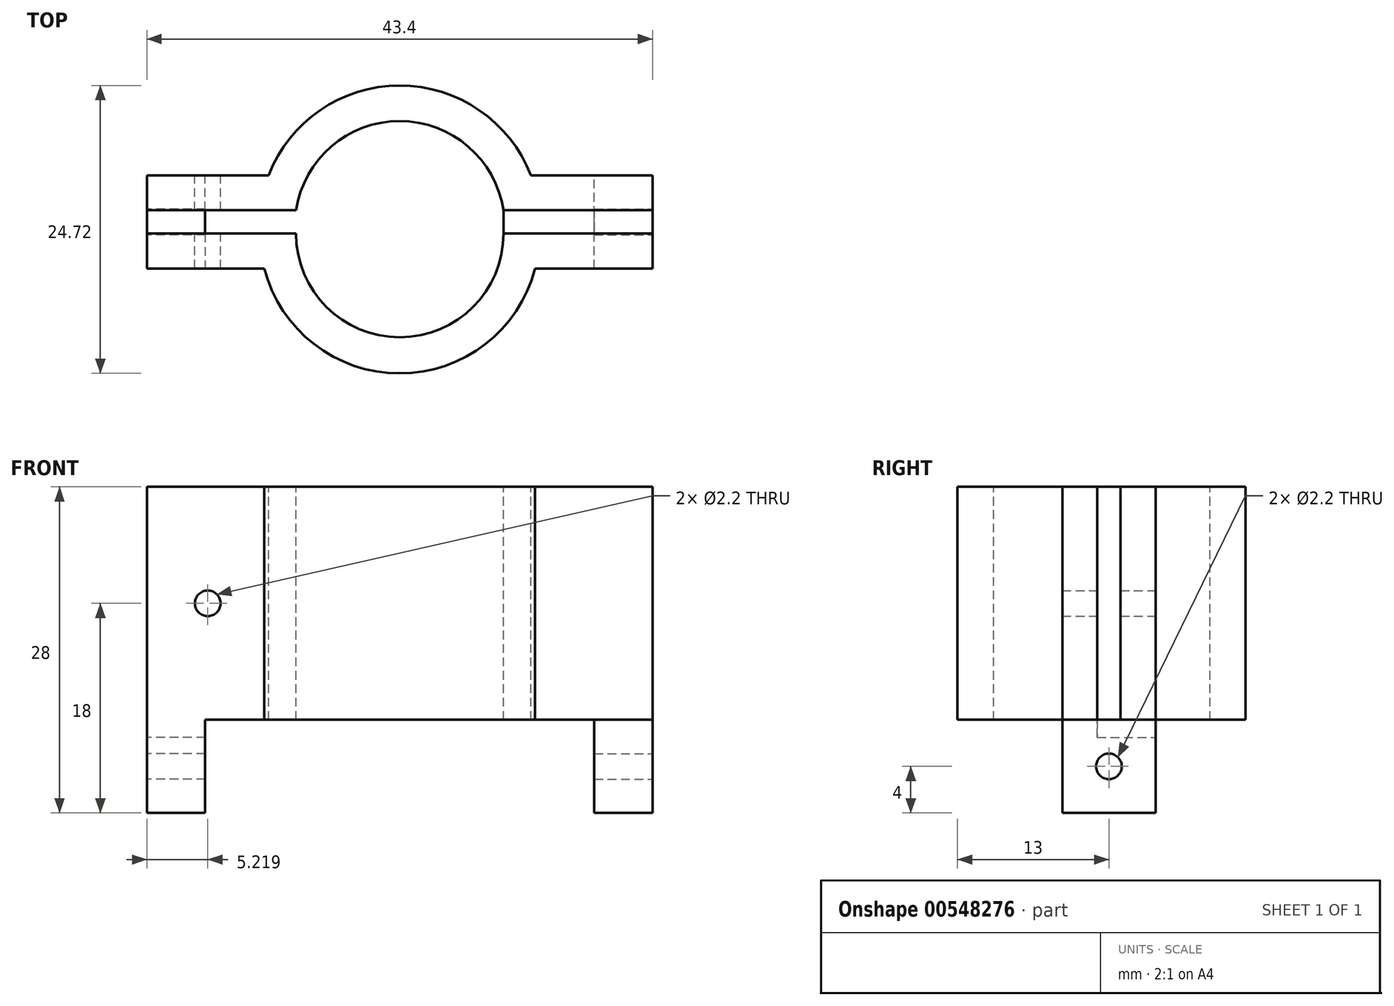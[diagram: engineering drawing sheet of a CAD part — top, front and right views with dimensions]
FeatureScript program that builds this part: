
annotation { "Feature Type Name" : "Feature", "Feature Type Description" : "" }
export const myFeature = defineFeature(function(context is Context, id is Id, definition is map)
    precondition{}
    {
        {
            var Q0;
            Q0=qCreatedBy(makeId("Top.planeOp"),FACE);
            var sketch = newSketch(context, id + "F0", { "sketchPlane" : qUnion([Q0])});
            skArc(sketch, "E0", {"start": v(-8.9, 0) * mm, "mid": v(0, -8.9) * mm, "end": v(8.9, 0) * mm});
            skArc(sketch, "E1", {"start": v(-12, 0) * mm, "mid": v(0, -12) * mm, "end": v(12, 0) * mm});
            skLineSegment(sketch, "E2.bottom", {"start": v(-8.9, 0) * mm, "end": v(-21.7, 0) * mm});
            skLineSegment(sketch, "E2.top", {"start": v(-8.9, -3) * mm, "end": v(-21.7, -3) * mm});
            skLineSegment(sketch, "E2.left", {"start": v(-8.9, 0) * mm, "end": v(-8.9, -3) * mm});
            skLineSegment(sketch, "E2.right", {"start": v(-21.7, 0) * mm, "end": v(-21.7, -3) * mm});
            skLineSegment(sketch, "E3.bottom", {"start": v(8.9, 0) * mm, "end": v(21.7, 0) * mm});
            skLineSegment(sketch, "E3.top", {"start": v(8.9, -3) * mm, "end": v(21.7, -3) * mm});
            skLineSegment(sketch, "E3.left", {"start": v(8.9, 0) * mm, "end": v(8.9, -3) * mm});
            skLineSegment(sketch, "E3.right", {"start": v(21.7, 0) * mm, "end": v(21.7, -3) * mm});
            skSolve(sketch);
        }
        {
            var Q0;
            Q0=qSketchRegion(id+"F0",true);
            extrude(context, id + "F1", {"entities" : qUnion([Q0]), "oppositeDirection" : true, "depth" : 20 * mm, "offsetDistance" : 25 * mm});
        }
        {
            var Q0;
            Q0=makeQuery(id+"F1.opExtrude","SWEPT_FACE",FACE,{"disambiguationData":[OSD([sQuery(id+"F0.wireOp",EDGE,"E3.right")])]});
            var sketch = newSketch(context, id + "F2", { "sketchPlane" : qUnion([Q0])});
            skPoint(sketch, "E4.oppositeSnap0", {"position": v(-1.5, 0) * mm});
            skLineSegment(sketch, "E4.bottom", {"start": v(0, -20) * mm, "end": v(2, -20) * mm});
            skLineSegment(sketch, "E4.top", {"start": v(0, 0) * mm, "end": v(2, 0) * mm});
            skLineSegment(sketch, "E4.left", {"start": v(0, -20) * mm, "end": v(0, 0) * mm});
            skLineSegment(sketch, "E4.right", {"start": v(2, -20) * mm, "end": v(2, 0) * mm});
            skLineSegment(sketch, "E5.bottom", {"start": v(-3, -20) * mm, "end": v(5, -20) * mm});
            skLineSegment(sketch, "E5.top", {"start": v(-3, -28) * mm, "end": v(5, -28) * mm});
            skLineSegment(sketch, "E5.left", {"start": v(-3, -20) * mm, "end": v(-3, -28) * mm});
            skLineSegment(sketch, "E5.right", {"start": v(5, -20) * mm, "end": v(5, -28) * mm});
            skCircle(sketch, "E6", {"center": v(1, -24) * mm, "radius": 1.1 * mm});
            skSolve(sketch);
        }
        {
            var Q0;
            Q0=qCreatedBy(makeId("Top.planeOp"),FACE);
            var sketch = newSketch(context, id + "F3", { "sketchPlane" : qUnion([Q0])});
            skArc(sketch, "E7", {"start": v(8.9, 2) * mm, "mid": v(0, 9.66) * mm, "end": v(-8.9, 2) * mm});
            skLineSegment(sketch, "E8.bottom", {"start": v(-8.9, 2) * mm, "end": v(-21.7, 2) * mm});
            skLineSegment(sketch, "E8.top", {"start": v(-8.9, 5) * mm, "end": v(-21.7, 5) * mm});
            skLineSegment(sketch, "E8.left", {"start": v(-8.9, 2) * mm, "end": v(-8.9, 5) * mm});
            skLineSegment(sketch, "E8.right", {"start": v(-21.7, 2) * mm, "end": v(-21.7, 5) * mm});
            skLineSegment(sketch, "E9.bottom", {"start": v(8.9, 2) * mm, "end": v(21.7, 2) * mm});
            skLineSegment(sketch, "E9.top", {"start": v(8.9, 5) * mm, "end": v(21.7, 5) * mm});
            skLineSegment(sketch, "E9.left", {"start": v(8.9, 2) * mm, "end": v(8.9, 5) * mm});
            skLineSegment(sketch, "E9.right", {"start": v(21.7, 2) * mm, "end": v(21.7, 5) * mm});
            skArc(sketch, "E10", {"start": v(12, 2) * mm, "mid": v(0, 12.72) * mm, "end": v(-12, 2) * mm});
            skSolve(sketch);
        }
        {
            var Q0;
            {var subQ0=sQuery(id+"F3.wireOp",EDGE,"E8.right");Q0=makeQuery(id+"F3.imprint","IMPRINT",FACE,{"disambiguationData":[TD([[makeQuery(id+"F3.imprint","IMPRINT",EDGE,{"derivedFrom":subQ0}),-1.0]])]});}
            var Q1;
            {var subQ0=sQuery(id+"F3.wireOp",EDGE,"E8.left");Q1=makeQuery(id+"F3.imprint","IMPRINT",FACE,{"disambiguationData":[TD([[makeQuery(id+"F3.imprint","IMPRINT",EDGE,{"derivedFrom":subQ0}),1.0]])]});}
            var Q2;
            Q2=makeQuery(id+"F3.imprint","IMPRINT",FACE,{"disambiguationData":[TD([[makeQuery(id+"F3.imprint","IMPRINT",EDGE,{"derivedFrom":sQuery(id+"F3.wireOp",EDGE,"E7")}),-1.0]])]});
            var Q3;
            {var subQ0=sQuery(id+"F3.wireOp",EDGE,"E9.right");Q3=makeQuery(id+"F3.imprint","IMPRINT",FACE,{"disambiguationData":[TD([[makeQuery(id+"F3.imprint","IMPRINT",EDGE,{"derivedFrom":subQ0}),1.0]])]});}
            var Q4;
            {var subQ0=sQuery(id+"F3.wireOp",EDGE,"E9.left");Q4=makeQuery(id+"F3.imprint","IMPRINT",FACE,{"disambiguationData":[TD([[makeQuery(id+"F3.imprint","IMPRINT",EDGE,{"derivedFrom":subQ0}),-1.0]])]});}
            extrude(context, id + "F4", {"entities" : qUnion([Q0, Q1, Q2, Q3, Q4]), "oppositeDirection" : true, "depth" : 20 * mm, "offsetDistance" : 25 * mm});
        }
        {
            var Q0;
            Q0=makeQuery(id+"F2.imprint","IMPRINT",FACE,{"disambiguationData":[TD([[makeQuery(id+"F2.imprint","IMPRINT",EDGE,{"derivedFrom":sQuery(id+"F2.wireOp",EDGE,"E4.top")}),-1.0]])]});
            extrude(context, id + "F5", {"entities" : qUnion([Q0]), "oppositeDirection" : true, "depth" : 12.8 * mm, "offsetDistance" : 25 * mm});
        }
        {
            var Q0;
            Q0=makeQuery(id+"F2.imprint","IMPRINT",FACE,{"disambiguationData":[TD([[makeQuery(id+"F2.imprint","IMPRINT",EDGE,{"derivedFrom":sQuery(id+"F2.wireOp",EDGE,"E5.top")}),1.0]])]});
            extrude(context, id + "F6", {"entities" : qUnion([Q0]), "oppositeDirection" : true, "depth" : 5 * mm, "offsetDistance" : 25 * mm});
        }
        {
            var Q0;
            Q0=makeQuery(id+"F1.opExtrude","SWEPT_FACE",FACE,{"disambiguationData":[OSD([sQuery(id+"F0.wireOp",EDGE,"E2.right")])]});
            var sketch = newSketch(context, id + "F7", { "sketchPlane" : qUnion([Q0])});
            skLineSegment(sketch, "E11.bottom", {"start": v(3, -20) * mm, "end": v(0, -20) * mm});
            skLineSegment(sketch, "E11.top", {"start": v(3, -21.5) * mm, "end": v(0, -21.5) * mm});
            skLineSegment(sketch, "E11.left", {"start": v(3, -20) * mm, "end": v(3, -21.5) * mm});
            skLineSegment(sketch, "E11.right", {"start": v(0, -20) * mm, "end": v(0, -21.5) * mm});
            skLineSegment(sketch, "E12.bottom", {"start": v(3, -21.5) * mm, "end": v(-5, -21.5) * mm});
            skLineSegment(sketch, "E12.top", {"start": v(3, -28) * mm, "end": v(-5, -28) * mm});
            skLineSegment(sketch, "E12.left", {"start": v(3, -21.5) * mm, "end": v(3, -28) * mm});
            skLineSegment(sketch, "E12.right", {"start": v(-5, -21.5) * mm, "end": v(-5, -28) * mm});
            skCircle(sketch, "E13", {"center": v(-1, -24) * mm, "radius": 1.1 * mm});
            skSolve(sketch);
        }
        {
            var Q0;
            Q0=qSketchRegion(id+"F7",true);
            extrude(context, id + "F8", {"entities" : qUnion([Q0]), "operationType" : NewBodyOperationType.ADD, "oppositeDirection" : true, "depth" : 5 * mm, "offsetDistance" : 25 * mm});
        }
        {
            var Q0;
            Q0=makeQuery(id+"F4.opExtrude","SWEPT_FACE",FACE,{"disambiguationData":[OSD([sQuery(id+"F3.wireOp",EDGE,"E8.top")])]});
            var sketch = newSketch(context, id + "F9", { "sketchPlane" : qUnion([Q0])});
            skCircle(sketch, "E14", {"center": v(16.48, -10) * mm, "radius": 1.1 * mm});
            skSolve(sketch);
        }
        {
            var Q0;
            Q0=sQuery(id+"F9.wireOp",VERTEX,"E14.center");
            var Q1;
            Q1=makeQuery(id+"F1.opExtrude","SWEPT_BODY",BODY,{"disambiguationData":[OSD([sQuery(id+"F0.wireOp",EDGE,"E0"),sQuery(id+"F0.wireOp",EDGE,"E1"),sQuery(id+"F0.wireOp",EDGE,"E2.bottom"),sQuery(id+"F0.wireOp",EDGE,"E2.top"),sQuery(id+"F0.wireOp",EDGE,"E2.right"),sQuery(id+"F0.wireOp",EDGE,"E3.bottom"),sQuery(id+"F0.wireOp",EDGE,"E3.top"),sQuery(id+"F0.wireOp",EDGE,"E3.right")])]});
            var Q2;
            Q2=makeQuery(id+"F4.opExtrude","SWEPT_BODY",BODY,{"disambiguationData":[OSD([sQuery(id+"F3.wireOp",EDGE,"E7"),sQuery(id+"F3.wireOp",EDGE,"E8.bottom"),sQuery(id+"F3.wireOp",EDGE,"E8.top"),sQuery(id+"F3.wireOp",EDGE,"E8.right"),sQuery(id+"F3.wireOp",EDGE,"E9.bottom"),sQuery(id+"F3.wireOp",EDGE,"E9.top"),sQuery(id+"F3.wireOp",EDGE,"E9.right"),sQuery(id+"F3.wireOp",EDGE,"E10")])]});
            hole(context, id + "F10", {"style" : HoleStyle.SIMPLE, "endStyle" : HoleEndStyle.THROUGH, "holeDiameter" : 2.2 * mm, "isTappedThrough" : true, "tappedDepth" : 12 * mm, "tapClearance" : 3, "locations" : qUnion([Q0]), "scope" : qUnion([Q1, Q2])});
        }
    });
